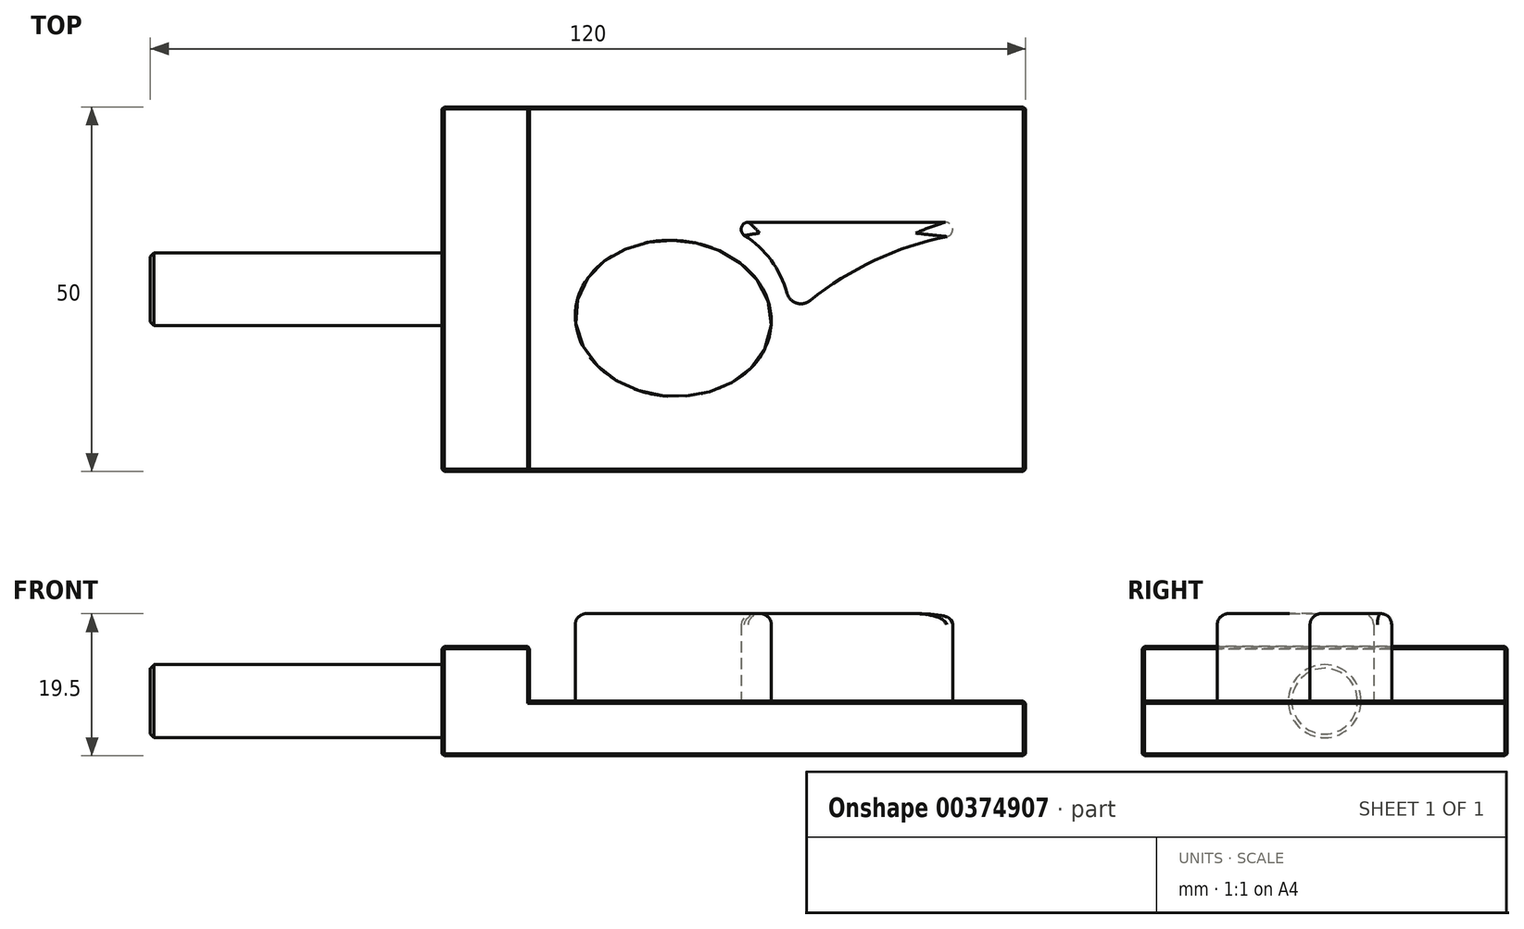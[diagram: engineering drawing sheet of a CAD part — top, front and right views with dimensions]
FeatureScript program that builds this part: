
annotation { "Feature Type Name" : "Feature", "Feature Type Description" : "" }
export const myFeature = defineFeature(function(context is Context, id is Id, definition is map)
    precondition{}
    {
        {
            var Q0;
            Q0=qCreatedBy(makeId("Top.planeOp"),FACE);
            var sketch = newSketch(context, id + "F0", { "sketchPlane" : qUnion([Q0])});
            skLineSegment(sketch, "E0.bottom", {"start": v(40, -25) * mm, "end": v(-40, -25) * mm});
            skLineSegment(sketch, "E0.top", {"start": v(40, 25) * mm, "end": v(-40, 25) * mm});
            skLineSegment(sketch, "E0.left", {"start": v(40, -25) * mm, "end": v(40, 25) * mm});
            skLineSegment(sketch, "E0.right", {"start": v(-40, -25) * mm, "end": v(-40, 25) * mm});
            skPoint(sketch, "E0.middle", {"position": v(0, 0) * mm});
            skSolve(sketch);
        }
        {
            var Q0;
            Q0 = qSketchRegion(id + "F0", true);
            extrude(context, id + "F1", {"entities" : qUnion([Q0]), "depth" : 7.5 * mm});
        }
        {
            var Q0;
            Q0=makeQuery(id+"F1.opExtrude","CAP_FACE",FACE,{"disambiguationData":[OSD([sQuery(id+"F0.wireOp",EDGE,"E0.bottom"),sQuery(id+"F0.wireOp",EDGE,"E0.top"),sQuery(id+"F0.wireOp",EDGE,"E0.left"),sQuery(id+"F0.wireOp",EDGE,"E0.right")])],"isStart":false});
            var sketch = newSketch(context, id + "F2", { "sketchPlane" : qUnion([Q0])});
            skLineSegment(sketch, "E1.bottom", {"start": v(-40, 25) * mm, "end": v(-28, 25) * mm});
            skLineSegment(sketch, "E1.top", {"start": v(-40, -25) * mm, "end": v(-28, -25) * mm});
            skLineSegment(sketch, "E1.left", {"start": v(-40, 25) * mm, "end": v(-40, -25) * mm});
            skLineSegment(sketch, "E1.right", {"start": v(-28, 25) * mm, "end": v(-28, -25) * mm});
            skSolve(sketch);
        }
        {
            var Q0;
            Q0 = qSketchRegion(id + "F2", true);
            extrude(context, id + "F3", {"entities" : qUnion([Q0]), "operationType" : NewBodyOperationType.ADD, "depth" : 7.5 * mm});
        }
        {
            var Q0;
            Q0=makeQuery(id+"F3.boolean.opBoolean","MERGE",FACE,{"derivedFrom":[makeQuery(id+"F1.opExtrude","SWEPT_FACE",FACE,{"disambiguationData":[OSD([sQuery(id+"F0.wireOp",EDGE,"E0.right")])]}),makeQuery(id+"F3.opExtrude","SWEPT_FACE",FACE,{"disambiguationData":[OSD([sQuery(id+"F2.wireOp",EDGE,"E1.left")])]})]});
            var sketch = newSketch(context, id + "F4", { "sketchPlane" : qUnion([Q0])});
            skCircle(sketch, "E2", {"center": v(0, 7.5) * mm, "radius": 5 * mm});
            skSolve(sketch);
        }
        {
            var Q0;
            Q0 = qSketchRegion(id + "F4", true);
            extrude(context, id + "F5", {"entities" : qUnion([Q0]), "operationType" : NewBodyOperationType.ADD, "depth" : 40 * mm});
        }
        {
            var Q0;
            Q0=makeQuery(id+"F1.opExtrude","CAP_FACE",FACE,{"disambiguationData":[OSD([sQuery(id+"F0.wireOp",EDGE,"E0.bottom"),sQuery(id+"F0.wireOp",EDGE,"E0.top"),sQuery(id+"F0.wireOp",EDGE,"E0.left"),sQuery(id+"F0.wireOp",EDGE,"E0.right")])],"isStart":false});
            var sketch = newSketch(context, id + "F6", { "sketchPlane" : qUnion([Q0])});
            skPoint(sketch, "E3.endSnap0", {"position": v(9.9, -7) * mm});
            skLineSegment(sketch, "E4", {"start": v(-39.73, 25) * mm, "end": v(-47.82, 25) * mm, "construction": true});
            skEllipse(sketch, "E5", {"center": v(-8.3, -4) * mm, "majorRadius": 13.45 * mm, "minorRadius": 10.7 * mm, "majorAxis": v(1, -0.07)});
            skLineSegment(sketch, "E6", {"start": v(-8.3, -4) * mm, "end": v(-21.72, -3.06) * mm, "construction": true});
            skLineSegment(sketch, "E7", {"start": v(-20.22, 15) * mm, "end": v(22.21, 15) * mm, "construction": true});
            skSolve(sketch);
        }
        {
            var Q0;
            Q0 = qSketchRegion(id + "F6", true);
            extrude(context, id + "F7", {"entities" : qUnion([Q0]), "operationType" : NewBodyOperationType.ADD, "depth" : 12 * mm});
        }
        {
            var Q0;
            Q0=makeQuery(id+"F1.opExtrude","CAP_FACE",FACE,{"disambiguationData":[OSD([sQuery(id+"F0.wireOp",EDGE,"E0.bottom"),sQuery(id+"F0.wireOp",EDGE,"E0.top"),sQuery(id+"F0.wireOp",EDGE,"E0.left"),sQuery(id+"F0.wireOp",EDGE,"E0.right")])],"isStart":false});
            var sketch = newSketch(context, id + "F8", { "sketchPlane" : qUnion([Q0])});
            skLineSegment(sketch, "E8", {"start": v(2, 9.2) * mm, "end": v(29, 9.2) * mm});
            skArc(sketch, "E9", {"start": v(29, 9.2) * mm, "mid": v(30, 8.3) * mm, "end": v(29.2, 7.22) * mm});
            skArc(sketch, "E10", {"start": v(29.2, 7.22) * mm, "mid": v(19.3, 3.96) * mm, "end": v(10.45, -1.56) * mm});
            skArc(sketch, "E11", {"start": v(2, 9.2) * mm, "mid": v(1.04, 8.48) * mm, "end": v(1.46, 7.36) * mm});
            skLineSegment(sketch, "E12", {"start": v(-24.37, 15) * mm, "end": v(32.78, 15) * mm, "construction": true});
            skArc(sketch, "E13", {"start": v(7.27, -0.52) * mm, "mid": v(8.58, -1.9) * mm, "end": v(10.45, -1.56) * mm});
            skArc(sketch, "E14", {"start": v(7.27, -0.52) * mm, "mid": v(5.1, 3.96) * mm, "end": v(1.46, 7.36) * mm});
            skPoint(sketch, "E15.endSnap0", {"position": v(1.04, 8.48) * mm});
            skLineSegment(sketch, "E16", {"start": v(-5.76, -4.05) * mm, "end": v(-22.39, -2.88) * mm, "construction": true});
            skSolve(sketch);
        }
        {
            var Q0;
            Q0=makeQuery(id+"F5.opExtrude","CAP_EDGE",EDGE,{"disambiguationData":[OSD([sQuery(id+"F4.wireOp",EDGE,"E2")])],"isStart":false});
            chamfer(context, id + "F9", {"entities" : qUnion([Q0]), "width" : 0.5 * mm, "tangentPropagation" : true});
        }
        {
            var Q0;
            Q0=makeQuery(id+"F3.opExtrude","CAP_EDGE",EDGE,{"disambiguationData":[OSD([sQuery(id+"F2.wireOp",EDGE,"E1.bottom")])],"isStart":false});
            var Q1;
            Q1=makeQuery(id+"F3.opExtrude","CAP_EDGE",EDGE,{"disambiguationData":[OSD([sQuery(id+"F2.wireOp",EDGE,"E1.right")])],"isStart":false});
            var Q2;
            Q2=makeQuery(id+"F3.opExtrude","CAP_EDGE",EDGE,{"disambiguationData":[OSD([sQuery(id+"F2.wireOp",EDGE,"E1.top")])],"isStart":false});
            var Q3;
            Q3=makeQuery(id+"F3.opExtrude","CAP_EDGE",EDGE,{"disambiguationData":[OSD([sQuery(id+"F2.wireOp",EDGE,"E1.left")])],"isStart":false});
            var Q4;
            Q4=makeQuery(id+"F1.opExtrude","CAP_EDGE",EDGE,{"disambiguationData":[OSD([sQuery(id+"F0.wireOp",EDGE,"E0.top")])],"isStart":false});
            var Q5;
            Q5=makeQuery(id+"F1.opExtrude","CAP_EDGE",EDGE,{"disambiguationData":[OSD([sQuery(id+"F0.wireOp",EDGE,"E0.left")])],"isStart":false});
            var Q6;
            Q6=makeQuery(id+"F1.opExtrude","CAP_EDGE",EDGE,{"disambiguationData":[OSD([sQuery(id+"F0.wireOp",EDGE,"E0.bottom")])],"isStart":false});
            var Q7;
            Q7=makeQuery(id+"F3.opExtrude","SWEPT_EDGE",EDGE,{"disambiguationData":[OSD([sQuery(id+"F0.wireOp",EDGE,"E0.bottom"),sQuery(id+"F2.wireOp",EDGE,"E1.top"),sQuery(id+"F2.wireOp",EDGE,"E1.right")])]});
            var Q8;
            Q8=makeQuery(id+"F3.opExtrude","SWEPT_EDGE",EDGE,{"disambiguationData":[OSD([sQuery(id+"F0.wireOp",EDGE,"E0.top"),sQuery(id+"F2.wireOp",EDGE,"E1.bottom"),sQuery(id+"F2.wireOp",EDGE,"E1.right")])]});
            var Q9;
            Q9=makeQuery(id+"F1.opExtrude","SWEPT_EDGE",EDGE,{"disambiguationData":[OSD([sQuery(id+"F0.wireOp",EDGE,"E0.bottom"),sQuery(id+"F0.wireOp",EDGE,"E0.left")])]});
            var Q10;
            Q10=makeQuery(id+"F1.opExtrude","SWEPT_EDGE",EDGE,{"disambiguationData":[OSD([sQuery(id+"F0.wireOp",EDGE,"E0.top"),sQuery(id+"F0.wireOp",EDGE,"E0.left")])]});
            var Q11;
            Q11=makeQuery(id+"F3.boolean.opBoolean","MERGE",EDGE,{"derivedFrom":[makeQuery(id+"F1.opExtrude","SWEPT_EDGE",EDGE,{"disambiguationData":[OSD([sQuery(id+"F0.wireOp",EDGE,"E0.bottom"),sQuery(id+"F0.wireOp",EDGE,"E0.right")])]}),makeQuery(id+"F3.opExtrude","SWEPT_EDGE",EDGE,{"disambiguationData":[OSD([sQuery(id+"F2.wireOp",EDGE,"E1.top"),sQuery(id+"F2.wireOp",EDGE,"E1.left")])]})]});
            var Q12;
            Q12=makeQuery(id+"F3.boolean.opBoolean","MERGE",EDGE,{"derivedFrom":[makeQuery(id+"F1.opExtrude","SWEPT_EDGE",EDGE,{"disambiguationData":[OSD([sQuery(id+"F0.wireOp",EDGE,"E0.top"),sQuery(id+"F0.wireOp",EDGE,"E0.right")])]}),makeQuery(id+"F3.opExtrude","SWEPT_EDGE",EDGE,{"disambiguationData":[OSD([sQuery(id+"F2.wireOp",EDGE,"E1.bottom"),sQuery(id+"F2.wireOp",EDGE,"E1.left")])]})]});
            var Q13;
            Q13=makeQuery(id+"F1.opExtrude","CAP_EDGE",EDGE,{"disambiguationData":[OSD([sQuery(id+"F0.wireOp",EDGE,"E0.right")])],"isStart":true});
            var Q14;
            Q14=makeQuery(id+"F1.opExtrude","CAP_EDGE",EDGE,{"disambiguationData":[OSD([sQuery(id+"F0.wireOp",EDGE,"E0.bottom")])],"isStart":true});
            var Q15;
            Q15=makeQuery(id+"F1.opExtrude","CAP_EDGE",EDGE,{"disambiguationData":[OSD([sQuery(id+"F0.wireOp",EDGE,"E0.left")])],"isStart":true});
            var Q16;
            Q16=makeQuery(id+"F1.opExtrude","CAP_EDGE",EDGE,{"disambiguationData":[OSD([sQuery(id+"F0.wireOp",EDGE,"E0.top")])],"isStart":true});
            chamfer(context, id + "F10", {"entities" : qUnion([Q0, Q1, Q2, Q3, Q4, Q5, Q6, Q7, Q8, Q9, Q10, Q11, Q12, Q13, Q14, Q15, Q16]), "width" : 0.3 * mm, "tangentPropagation" : true});
        }
        {
            var Q0;
            Q0=makeQuery(id+"F7.opExtrude","CAP_EDGE",EDGE,{"disambiguationData":[OSD([sQuery(id+"F6.wireOp",EDGE,"E5")])],"isStart":false});
            fillet(context, id + "F11", {"entities" : qUnion([Q0]), "radius" : 1.5 * mm, "tangentPropagation" : true, "allowEdgeOverflow" : false});
        }
        {
            var Q0;
            Q0 = qSketchRegion(id + "F8", true);
            extrude(context, id + "F12", {"entities" : qUnion([Q0]), "operationType" : NewBodyOperationType.ADD, "depth" : 12 * mm});
        }
        {
            var Q0;
            Q0=makeQuery(id+"F12.opExtrude","CAP_EDGE",EDGE,{"disambiguationData":[OSD([sQuery(id+"F8.wireOp",EDGE,"E8")])],"isStart":false});
            var Q1;
            Q1=makeQuery(id+"F12.opExtrude","CAP_EDGE",EDGE,{"disambiguationData":[OSD([sQuery(id+"F8.wireOp",EDGE,"E9")])],"isStart":false});
            var Q2;
            Q2=makeQuery(id+"F12.opExtrude","CAP_EDGE",EDGE,{"disambiguationData":[OSD([sQuery(id+"F8.wireOp",EDGE,"E10")])],"isStart":false});
            var Q3;
            Q3=makeQuery(id+"F12.opExtrude","CAP_EDGE",EDGE,{"disambiguationData":[OSD([sQuery(id+"F8.wireOp",EDGE,"E13")])],"isStart":false});
            var Q4;
            Q4=makeQuery(id+"F12.opExtrude","CAP_EDGE",EDGE,{"disambiguationData":[OSD([sQuery(id+"F8.wireOp",EDGE,"E14")])],"isStart":false});
            var Q5;
            Q5=makeQuery(id+"F12.opExtrude","CAP_EDGE",EDGE,{"disambiguationData":[OSD([sQuery(id+"F8.wireOp",EDGE,"E11")])],"isStart":false});
            fillet(context, id + "F13", {"entities" : qUnion([Q0, Q1, Q2, Q3, Q4, Q5]), "radius" : 1.5 * mm, "tangentPropagation" : true, "allowEdgeOverflow" : false});
        }
    });
